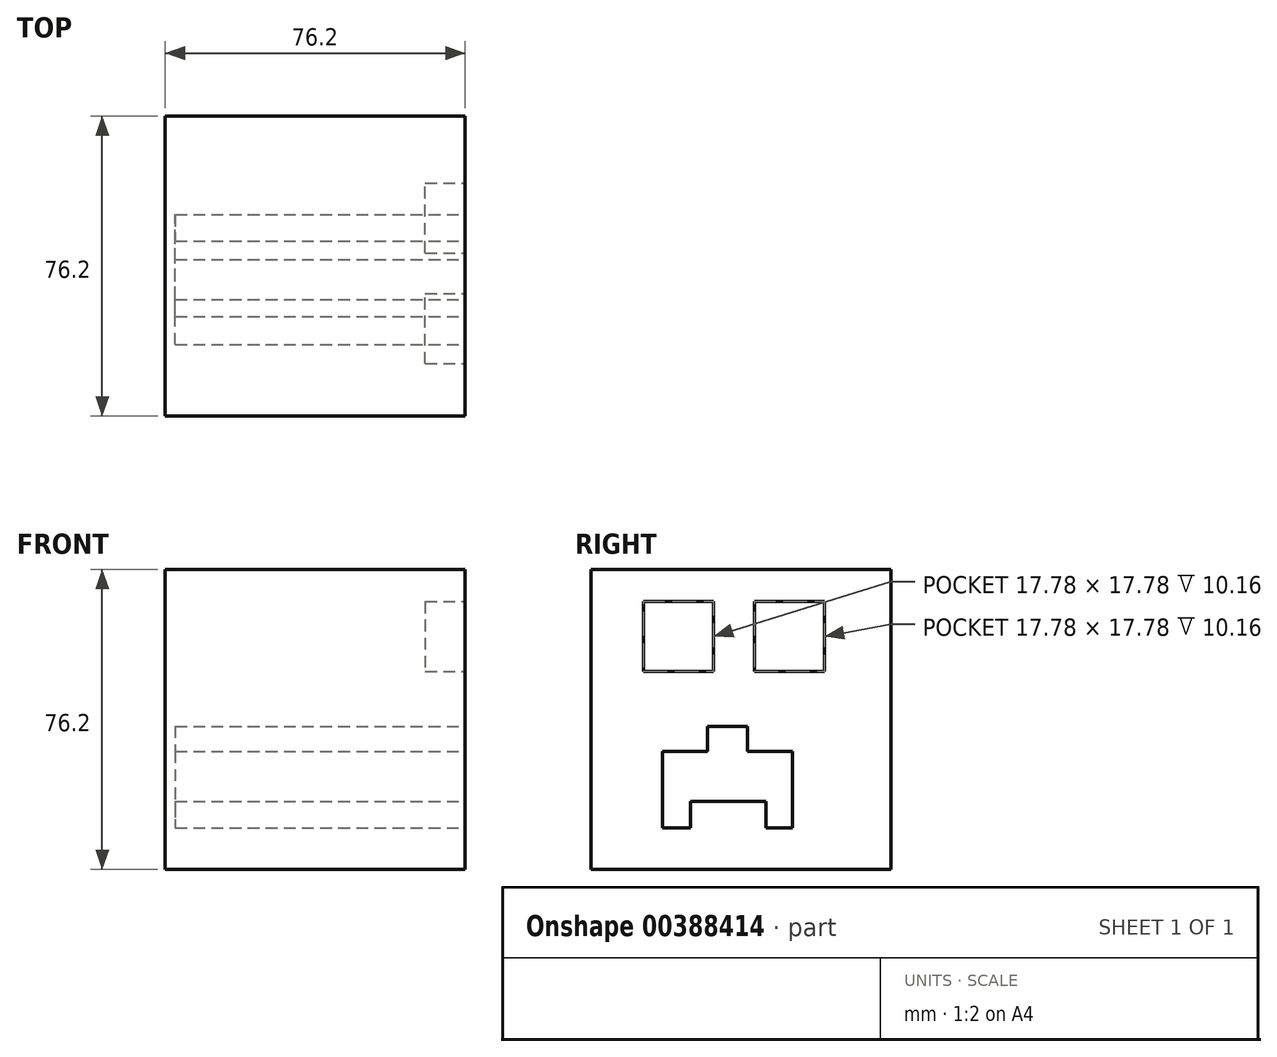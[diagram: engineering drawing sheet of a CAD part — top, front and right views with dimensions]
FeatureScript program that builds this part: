
annotation { "Feature Type Name" : "Feature", "Feature Type Description" : "" }
export const myFeature = defineFeature(function(context is Context, id is Id, definition is map)
    precondition{}
    {
        {
            var Q0;
            Q0=qCreatedBy(makeId("Top.planeOp"),FACE);
            var sketch = newSketch(context, id + "F0", { "sketchPlane" : qUnion([Q0])});
            skLineSegment(sketch, "E0.bottom", {"start": v(-38.1, 38.1) * mm, "end": v(38.1, 38.1) * mm});
            skLineSegment(sketch, "E0.top", {"start": v(-38.1, -38.1) * mm, "end": v(38.1, -38.1) * mm});
            skLineSegment(sketch, "E0.left", {"start": v(-38.1, 38.1) * mm, "end": v(-38.1, -38.1) * mm});
            skLineSegment(sketch, "E0.right", {"start": v(38.1, 38.1) * mm, "end": v(38.1, -38.1) * mm});
            skPoint(sketch, "E0.middle", {"position": v(0, 0) * mm});
            skSolve(sketch);
        }
        {
            var Q0;
            Q0=makeQuery(id+"F0.imprint","IMPRINT",FACE,{"disambiguationData":[TD([[makeQuery(id+"F0.imprint","IMPRINT",EDGE,{"derivedFrom":sQuery(id+"F0.wireOp",EDGE,"E0.bottom")}),-1.0]])]});
            extrude(context, id + "F1", {"entities" : qUnion([Q0]), "depth" : 76.2 * mm});
        }
        {
            var Q0;
            Q0=makeQuery(id+"F1.opExtrude","SWEPT_FACE",FACE,{"disambiguationData":[OSD([sQuery(id+"F0.wireOp",EDGE,"E0.right")])]});
            var sketch = newSketch(context, id + "F2", { "sketchPlane" : qUnion([Q0])});
            skLineSegment(sketch, "E1.bottom", {"start": v(-24.8, 68.06) * mm, "end": v(-7.03, 68.06) * mm});
            skLineSegment(sketch, "E1.top", {"start": v(-24.8, 50.28) * mm, "end": v(-7.03, 50.28) * mm});
            skLineSegment(sketch, "E1.left", {"start": v(-24.8, 68.06) * mm, "end": v(-24.8, 50.28) * mm});
            skLineSegment(sketch, "E1.right", {"start": v(-7.03, 68.06) * mm, "end": v(-7.03, 50.28) * mm});
            skPoint(sketch, "E1.middle", {"position": v(-15.92, 59.17) * mm});
            skLineSegment(sketch, "E2.bottom", {"start": v(3.36, 68.06) * mm, "end": v(21.14, 68.06) * mm});
            skLineSegment(sketch, "E2.top", {"start": v(3.36, 50.28) * mm, "end": v(21.14, 50.28) * mm});
            skLineSegment(sketch, "E2.left", {"start": v(3.36, 68.06) * mm, "end": v(3.36, 50.28) * mm});
            skLineSegment(sketch, "E2.right", {"start": v(21.14, 68.06) * mm, "end": v(21.14, 50.28) * mm});
            skPoint(sketch, "E2.middle", {"position": v(12.25, 59.17) * mm});
            skLineSegment(sketch, "E3.bottom", {"start": v(-8.54, 36.38) * mm, "end": v(1.62, 36.38) * mm});
            skLineSegment(sketch, "E3.left", {"start": v(-8.54, 36.38) * mm, "end": v(-8.54, 30.03) * mm});
            skLineSegment(sketch, "E3.right", {"start": v(1.62, 36.38) * mm, "end": v(1.62, 30.03) * mm});
            skPoint(sketch, "E3.middle", {"position": v(-3.46, 30.03) * mm});
            skLineSegment(sketch, "E4.bottom", {"start": v(-19.98, 30.03) * mm, "end": v(-8.54, 30.03) * mm});
            skLineSegment(sketch, "E4.top", {"start": v(-12.8, 17.33) * mm, "end": v(6.3, 17.33) * mm});
            skLineSegment(sketch, "E4.left", {"start": v(-19.98, 30.03) * mm, "end": v(-19.98, 17.33) * mm});
            skLineSegment(sketch, "E4.right", {"start": v(13.05, 30.03) * mm, "end": v(13.05, 17.33) * mm});
            skPoint(sketch, "E4.middle", {"position": v(-3.46, 23.68) * mm});
            skLineSegment(sketch, "E5.top", {"start": v(-19.98, 10.54) * mm, "end": v(-12.8, 10.54) * mm});
            skLineSegment(sketch, "E5.left", {"start": v(-19.98, 23.68) * mm, "end": v(-19.98, 10.54) * mm});
            skLineSegment(sketch, "E5.right", {"start": v(-12.8, 17.33) * mm, "end": v(-12.8, 10.54) * mm});
            skLineSegment(sketch, "E6.top", {"start": v(13.05, 10.54) * mm, "end": v(6.3, 10.54) * mm});
            skLineSegment(sketch, "E6.left", {"start": v(13.05, 23.68) * mm, "end": v(13.05, 10.54) * mm});
            skLineSegment(sketch, "E6.right", {"start": v(6.3, 17.33) * mm, "end": v(6.3, 10.54) * mm});
            skLineSegment(sketch, "E7.trimOffspring", {"start": v(1.62, 30.03) * mm, "end": v(13.05, 30.03) * mm});
            skPoint(sketch, "E8.orphan", {"position": v(1.62, 23.68) * mm});
            skPoint(sketch, "E9.orphan", {"position": v(-8.54, 23.68) * mm});
            skSolve(sketch);
        }
        {
            var Q0;
            Q0=makeQuery(id+"F1.opExtrude","SWEPT_FACE",FACE,{"disambiguationData":[OSD([sQuery(id+"F0.wireOp",EDGE,"E0.right")])]});
            shell(context, id + "F3", {"entities" : qUnion([Q0]), "thickness" : 2.54 * mm});
        }
        {
            var Q0;
            Q0=makeQuery(id+"F2.imprint","IMPRINT",FACE,{"disambiguationData":[TD([[makeQuery(id+"F2.imprint","IMPRINT",EDGE,{"derivedFrom":sQuery(id+"F2.wireOp",EDGE,"E1.bottom")}),1.0]])]});
            extrude(context, id + "F4", {"entities" : qUnion([Q0]), "operationType" : NewBodyOperationType.ADD, "oppositeDirection" : true, "depth" : 76.2 * mm});
        }
        {
            var Q0;
            Q0=makeQuery(id+"F4.boolean.opBoolean","SPLIT",FACE,{"disambiguationData":[TD([makeQuery(id+"F4.opExtrude","SWEPT_FACE",FACE,{"disambiguationData":[OSD([sQuery(id+"F2.wireOp",EDGE,"E1.bottom")])]})])],"derivedFrom":makeQuery(id+"F3.opShell","OFFSET_FACE",FACE,{"disambiguationData":[OSD([sQuery(id+"F0.wireOp",EDGE,"E0.left")])]})});
            var Q1;
            Q1=makeQuery(id+"F4.boolean.opBoolean","SPLIT",FACE,{"disambiguationData":[TD([makeQuery(id+"F4.opExtrude","SWEPT_FACE",FACE,{"disambiguationData":[OSD([sQuery(id+"F2.wireOp",EDGE,"E2.bottom")])]})])],"derivedFrom":makeQuery(id+"F3.opShell","OFFSET_FACE",FACE,{"disambiguationData":[OSD([sQuery(id+"F0.wireOp",EDGE,"E0.left")])]})});
            extrude(context, id + "F5", {"entities" : qUnion([Q0, Q1]), "operationType" : NewBodyOperationType.ADD, "depth" : 63.5 * mm});
        }
    });
